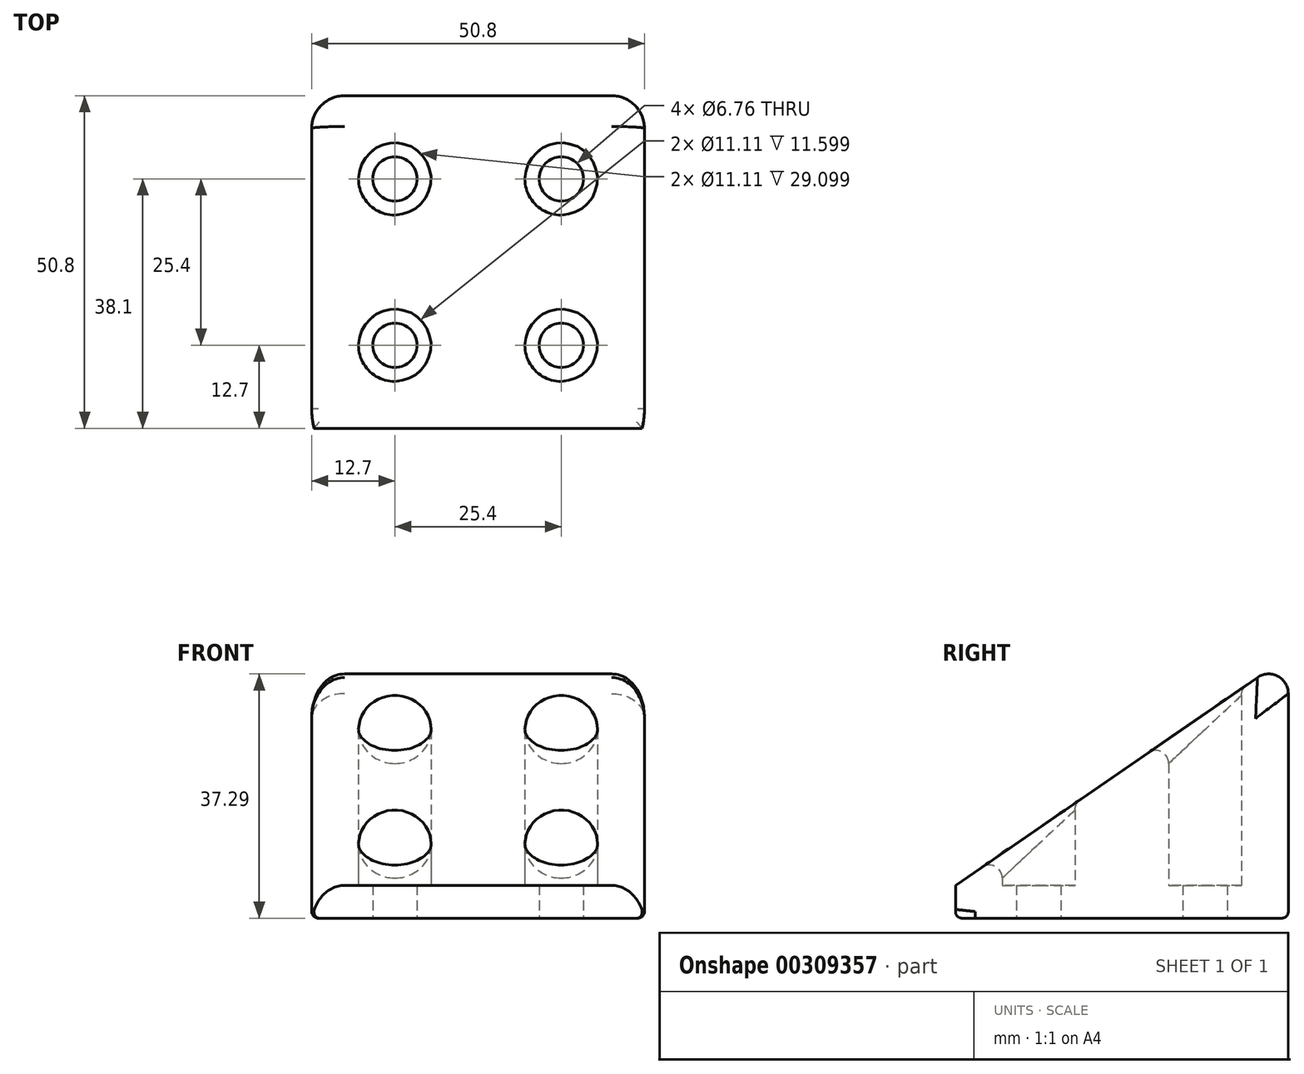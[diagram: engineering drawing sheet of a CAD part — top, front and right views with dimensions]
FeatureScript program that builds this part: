
annotation { "Feature Type Name" : "Feature", "Feature Type Description" : "" }
export const myFeature = defineFeature(function(context is Context, id is Id, definition is map)
    precondition{}
    {
        {
            var Q0;
            Q0=qCreatedBy(makeId("Right.planeOp"),FACE);
            var sketch = newSketch(context, id + "F0", { "sketchPlane" : qUnion([Q0])});
            skLineSegment(sketch, "E0.bottom", {"start": v(0, 0) * mm, "end": v(50.8, 0) * mm});
            skLineSegment(sketch, "E0.top", {"start": v(0, 40) * mm, "end": v(50.8, 40) * mm});
            skLineSegment(sketch, "E0.left", {"start": v(0, 0) * mm, "end": v(0, 40) * mm});
            skLineSegment(sketch, "E0.right", {"start": v(50.8, 0) * mm, "end": v(50.8, 40) * mm});
            skLineSegment(sketch, "E1", {"start": v(0, 0) * mm, "end": v(0, 5) * mm});
            skLineSegment(sketch, "E2", {"start": v(0, 5) * mm, "end": v(50.8, 40) * mm});
            skSolve(sketch);
        }
        {
            var Q0;
            Q0=makeQuery(id+"F0.imprint","IMPRINT",FACE,{"disambiguationData":[TD([[makeQuery(id+"F0.imprint","IMPRINT",EDGE,{"derivedFrom":sQuery(id+"F0.wireOp",EDGE,"E0.bottom")}),1.0]])]});
            extrude(context, id + "F1", {"entities" : qUnion([Q0]), "oppositeDirection" : true, "depth" : (25.4 * 2) * mm});
        }
        {
            var Q0;
            Q0=makeQuery(id+"F1.opExtrude","SWEPT_EDGE",EDGE,{"disambiguationData":[OSD([sQuery(id+"F0.wireOp",EDGE,"E0.top"),sQuery(id+"F0.wireOp",EDGE,"E0.right"),sQuery(id+"F0.wireOp",EDGE,"E2")])]});
            fillet(context, id + "F2", {"entities" : qUnion([Q0]), "radius" : 3 * mm, "tangentPropagation" : true, "allowEdgeOverflow" : false});
        }
        {
            var Q0;
            Q0=makeQuery(id+"F1.opExtrude","SWEPT_FACE",FACE,{"disambiguationData":[OSD([sQuery(id+"F0.wireOp",EDGE,"E0.bottom")])]});
            var sketch = newSketch(context, id + "F3", { "sketchPlane" : qUnion([Q0])});
            skLineSegment(sketch, "E3", {"start": v(-50.8, -50.8) * mm, "end": v(-38.1, -50.8) * mm});
            skLineSegment(sketch, "E4", {"start": v(-38.1, -50.8) * mm, "end": v(-12.7, -50.8) * mm});
            skLineSegment(sketch, "E5", {"start": v(-38.1, -50.8) * mm, "end": v(-38.1, -38.1) * mm});
            skLineSegment(sketch, "E6", {"start": v(-38.1, -38.1) * mm, "end": v(-38.1, -12.7) * mm});
            skLineSegment(sketch, "E7", {"start": v(-12.7, -50.8) * mm, "end": v(-12.7, -38.1) * mm});
            skLineSegment(sketch, "E8", {"start": v(-12.7, -38.1) * mm, "end": v(-12.7, -12.7) * mm});
            skCircle(sketch, "E9", {"center": v(-38.1, -12.7) * mm, "radius": 5.56 * mm});
            skCircle(sketch, "E10", {"center": v(-12.7, -12.7) * mm, "radius": 5.56 * mm});
            skCircle(sketch, "E11", {"center": v(-12.7, -38.1) * mm, "radius": 5.56 * mm});
            skCircle(sketch, "E12", {"center": v(-38.1, -38.1) * mm, "radius": 5.56 * mm});
            skSolve(sketch);
        }
        {
            var Q0;
            Q0=sQuery(id+"F3.wireOp",VERTEX,"E6.end");
            var Q1;
            Q1=sQuery(id+"F3.wireOp",VERTEX,"E6.start");
            var Q2;
            Q2=sQuery(id+"F3.wireOp",VERTEX,"E8.start");
            var Q3;
            Q3=sQuery(id+"F3.wireOp",VERTEX,"E8.end");
            var Q4;
            Q4=makeQuery(id+"F1.opExtrude","SWEPT_BODY",BODY,{"disambiguationData":[OSD([sQuery(id+"F0.wireOp",EDGE,"E0.bottom"),sQuery(id+"F0.wireOp",EDGE,"E0.right"),sQuery(id+"F0.wireOp",EDGE,"E1"),sQuery(id+"F0.wireOp",EDGE,"E2")])]});
            hole(context, id + "F4", {"style" : HoleStyle.SIMPLE, "endStyle" : HoleEndStyle.THROUGH, "standardTappedOrClearance" : lookupTablePath({ "standard" : "ANSI", "fit" : "Normal (ASME)", "size" : "1/4", "type" : "Clearance" }), "standardBlindInLast" : lookupTablePath({ "fit" : "Free", "standard" : "ANSI", "size" : "1/4", "type" : "Clearance" }), "holeDiameter" : 6.76 * mm, "tappedDepth" : 12 * mm, "tapClearance" : 3, "locations" : qUnion([Q0, Q1, Q2, Q3]), "scope" : qUnion([Q4])});
        }
        {
            var Q0;
            Q0=makeQuery(id+"F3.imprint","IMPRINT",FACE,{"disambiguationData":[TD([[makeQuery(id+"F3.imprint","IMPRINT",EDGE,{"derivedFrom":sQuery(id+"F3.wireOp",EDGE,"E9")}),1.0]])]});
            var Q1;
            {var subQ0=sQuery(id+"F3.wireOp",EDGE,"E6");var subQ1=sQuery(id+"F3.wireOp",EDGE,"E5");var subQ2=makeQuery(id+"F3.imprint","INTERSECT",VERTEX,{"derivedFrom":[subQ1,subQ0]});Q1=makeQuery(id+"F3.imprint","IMPRINT",FACE,{"disambiguationData":[TD([[makeQuery(id+"F3.imprint","IMPRINT",EDGE,{"disambiguationData":[TD([[subQ2,1.0]])],"derivedFrom":subQ1}),1.0]])]});}
            var Q2;
            {var subQ0=sQuery(id+"F3.wireOp",EDGE,"E6");var subQ1=sQuery(id+"F3.wireOp",EDGE,"E5");var subQ2=makeQuery(id+"F3.imprint","INTERSECT",VERTEX,{"derivedFrom":[subQ1,subQ0]});Q2=makeQuery(id+"F3.imprint","IMPRINT",FACE,{"disambiguationData":[TD([[makeQuery(id+"F3.imprint","IMPRINT",EDGE,{"disambiguationData":[TD([[subQ2,1.0]])],"derivedFrom":subQ1}),-1.0]])]});}
            var Q3;
            {var subQ0=sQuery(id+"F3.wireOp",EDGE,"E8");var subQ1=sQuery(id+"F3.wireOp",EDGE,"E7");var subQ2=makeQuery(id+"F3.imprint","INTERSECT",VERTEX,{"derivedFrom":[subQ1,subQ0]});Q3=makeQuery(id+"F3.imprint","IMPRINT",FACE,{"disambiguationData":[TD([[makeQuery(id+"F3.imprint","IMPRINT",EDGE,{"disambiguationData":[TD([[subQ2,1.0]])],"derivedFrom":subQ1}),1.0]])]});}
            var Q4;
            {var subQ0=sQuery(id+"F3.wireOp",EDGE,"E8");var subQ1=sQuery(id+"F3.wireOp",EDGE,"E7");var subQ2=makeQuery(id+"F3.imprint","INTERSECT",VERTEX,{"derivedFrom":[subQ1,subQ0]});Q4=makeQuery(id+"F3.imprint","IMPRINT",FACE,{"disambiguationData":[TD([[makeQuery(id+"F3.imprint","IMPRINT",EDGE,{"disambiguationData":[TD([[subQ2,1.0]])],"derivedFrom":subQ1}),-1.0]])]});}
            var Q5;
            Q5=makeQuery(id+"F3.imprint","IMPRINT",FACE,{"disambiguationData":[TD([[makeQuery(id+"F3.imprint","IMPRINT",EDGE,{"derivedFrom":sQuery(id+"F3.wireOp",EDGE,"E10")}),1.0]])]});
            extrude(context, id + "F5", {"entities" : qUnion([Q0, Q1, Q2, Q3, Q4, Q5]), "operationType" : NewBodyOperationType.REMOVE, "endBound" : BoundingType.THROUGH_ALL, "oppositeDirection" : true, "depth" : 40 * mm, "hasSecondDirection" : true, "secondDirectionOppositeDirection" : true, "secondDirectionDepth" : 5 * mm});
        }
        {
            var Q0;
            Q0=makeQuery(id+"F1.opExtrude","CAP_EDGE",EDGE,{"disambiguationData":[OSD([sQuery(id+"F0.wireOp",EDGE,"E0.right")])],"isStart":true});
            var Q1;
            Q1=makeQuery(id+"F1.opExtrude","CAP_EDGE",EDGE,{"disambiguationData":[OSD([sQuery(id+"F0.wireOp",EDGE,"E0.right")])],"isStart":false});
            fillet(context, id + "F6", {"entities" : qUnion([Q0, Q1]), "radius" : 5 * mm, "tangentPropagation" : true, "allowEdgeOverflow" : false});
        }
        {
            var Q0;
            Q0=makeQuery(id+"F5.boolean.opBoolean","INTERSECT",EDGE,{"derivedFrom":[makeQuery(id+"F1.opExtrude","SWEPT_FACE",FACE,{"disambiguationData":[OSD([sQuery(id+"F0.wireOp",EDGE,"E2")])]}),makeQuery(id+"F5.opExtrude","SWEPT_FACE",FACE,{"disambiguationData":[OSD([sQuery(id+"F3.wireOp",EDGE,"E12")])]})]});
            var Q1;
            Q1=makeQuery(id+"F5.boolean.opBoolean","INTERSECT",EDGE,{"derivedFrom":[makeQuery(id+"F1.opExtrude","SWEPT_FACE",FACE,{"disambiguationData":[OSD([sQuery(id+"F0.wireOp",EDGE,"E2")])]}),makeQuery(id+"F5.opExtrude","SWEPT_FACE",FACE,{"disambiguationData":[OSD([sQuery(id+"F3.wireOp",EDGE,"E11")])]})]});
            var Q2;
            Q2=makeQuery(id+"F5.boolean.opBoolean","INTERSECT",EDGE,{"derivedFrom":[makeQuery(id+"F1.opExtrude","SWEPT_FACE",FACE,{"disambiguationData":[OSD([sQuery(id+"F0.wireOp",EDGE,"E2")])]}),makeQuery(id+"F5.opExtrude","SWEPT_FACE",FACE,{"disambiguationData":[OSD([sQuery(id+"F3.wireOp",EDGE,"E10")])]})]});
            var Q3;
            Q3=makeQuery(id+"F5.boolean.opBoolean","INTERSECT",EDGE,{"derivedFrom":[makeQuery(id+"F1.opExtrude","SWEPT_FACE",FACE,{"disambiguationData":[OSD([sQuery(id+"F0.wireOp",EDGE,"E2")])]}),makeQuery(id+"F5.opExtrude","SWEPT_FACE",FACE,{"disambiguationData":[OSD([sQuery(id+"F3.wireOp",EDGE,"E9")])]})]});
            fillet(context, id + "F7", {"entities" : qUnion([Q0, Q1, Q2, Q3]), "radius" : 2 * mm, "tangentPropagation" : true, "allowEdgeOverflow" : false});
        }
        {
            var Q0;
            Q0=makeQuery(id+"F1.opExtrude","CAP_EDGE",EDGE,{"disambiguationData":[OSD([sQuery(id+"F0.wireOp",EDGE,"E0.bottom")])],"isStart":true});
            var Q1;
            Q1=makeQuery(id+"F1.opExtrude","SWEPT_EDGE",EDGE,{"disambiguationData":[OSD([sQuery(id+"F0.wireOp",EDGE,"E0.bottom"),sQuery(id+"F0.wireOp",EDGE,"E1")])]});
            fillet(context, id + "F8", {"entities" : qUnion([Q0, Q1]), "radius" : 1 * mm, "tangentPropagation" : true, "allowEdgeOverflow" : false});
        }
    });
